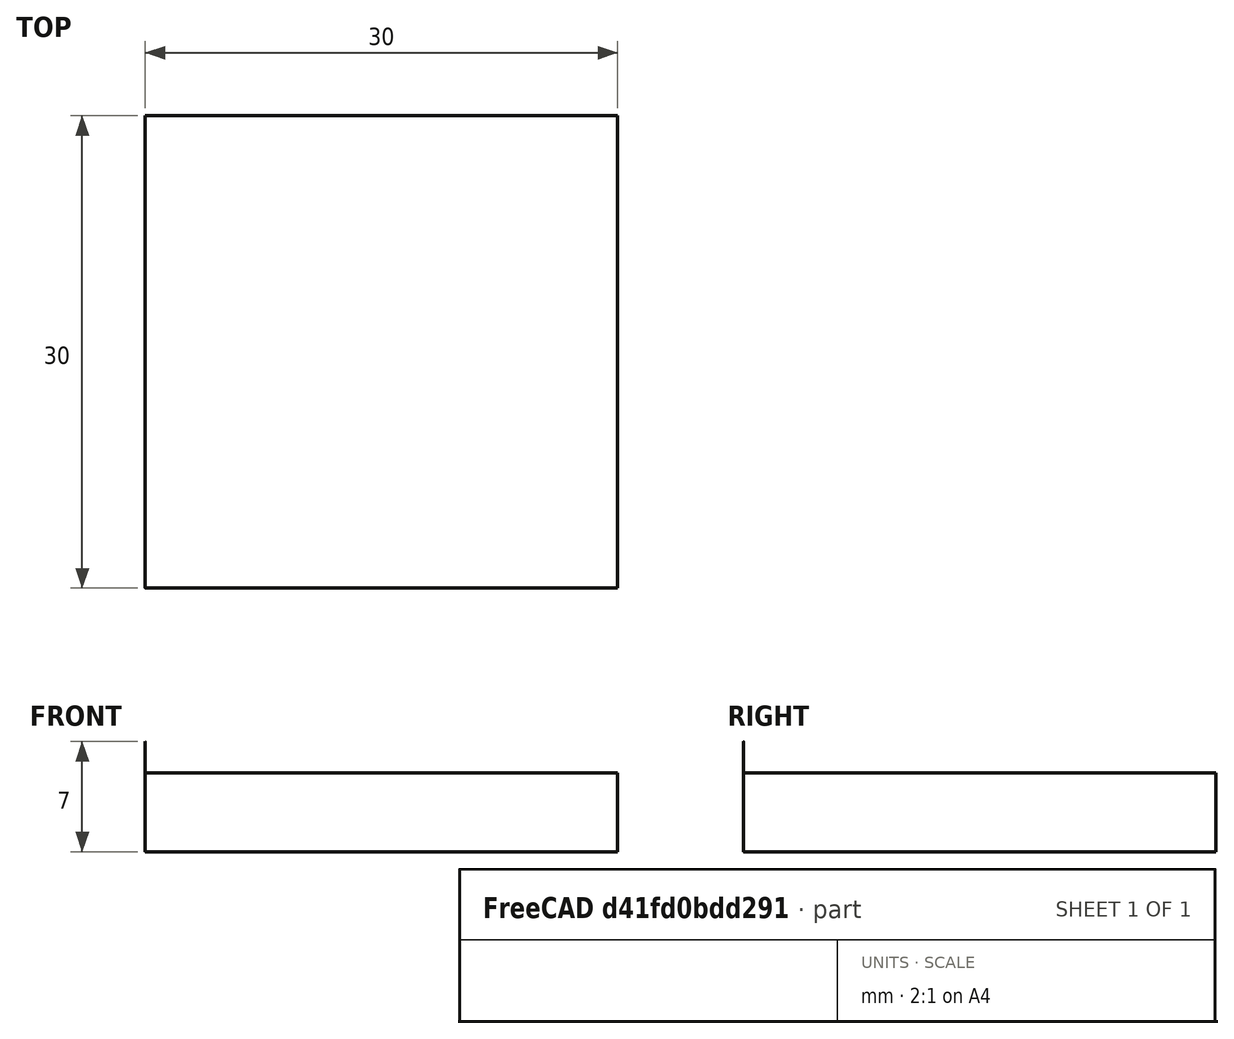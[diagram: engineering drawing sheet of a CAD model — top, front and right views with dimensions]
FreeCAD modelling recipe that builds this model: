
FCSTD DOCUMENT  (FreeCAD 1.0R39109 (Git))
Label: BoxWith2LargePockets
License: All rights reserved
LicenseURL: https://en.wikipedia.org/wiki/All_rights_reserved
objects: Path::FeaturePython×4, Part::Box×3, Part::FeaturePython×3, App::DocumentObjectGroup×3, Part::Cut×2, App::FeaturePython×1
note: 10 computed .brp shape members not serialized (recipe doc carries the construction recipe); baked Part::Feature solids carry a one-line shape summary decoded from their .brp

FEATURE [Part::Box] Box  label="Cube"
  AttacherType = Attacher::AttachEngine3D
  Height = 5
  Length = 30
  Width = 30
FEATURE [Part::Box] Box001  label="Cube001"
  AttacherType = Attacher::AttachEngine3D
  Height = 0.001
  Length = 10
  Placement = pos=(3,10,4.999) rot=(0,0,1;0rad)
  Width = 10
FEATURE [Part::Box] Box002  label="Cube002"
  AttacherType = Attacher::AttachEngine3D
  Height = 0.001
  Length = 10
  Placement = pos=(16,10,4.999) rot=(0,0,1;0rad)
  Width = 10
FEATURE [Part::Cut] Cut
  Base = -> Box
  Refine = true
  Tool = -> Box001
FEATURE [Part::Cut] Cut001
  Base = -> Cut
  Refine = true
  Tool = -> Box002
FEATURE [App::FeaturePython] SetupSheet  # Path/CAM operation (typed FeaturePython)
  ClearanceHeightExpression = OpStockZMax+SetupSheet.ClearanceHeightOffset
  ClearanceHeightOffset = 5
  CoolantMode = 0
  CoolantModes = None | Flood | Mist
  FinalDepthExpression = OpFinalDepth
  HorizRapid = 0
  SafeHeightExpression = OpStockZMax+SetupSheet.SafeHeightOffset
  SafeHeightOffset = 3
  StartDepthExpression = OpStartDepth
  StepDownExpression = OpToolDiameter
  VertRapid = 0
FEATURE [Part::FeaturePython] Clone  label="Model-Cut001"  # Draft clone (typed FeaturePython)
  AttacherType = Attacher::AttachEngine3D
  Fuse = false
  Objects = -> [Cut001]
  PathResource = Model
  Scale = (1,1,1)
FEATURE [App::DocumentObjectGroup] Model
  Group = -> [Clone]
FEATURE [Part::FeaturePython] ToolBit  label="Drill"  # Path/CAM toolbit (typed FeaturePython)
  BitPropertyNames = Chipload | Diameter | Flutes | Length | Material | TipAngle
  BitShape = <path>
  Chipload = 0
  Diameter = 0.005
  Flutes = 0
  Length = 7
  Material = 0
  ShapeName = drill
  TipAngle = 119
FEATURE [Path::FeaturePython] TC__Default_Tool  label="TC: Default Tool"  # Path/CAM operation (typed FeaturePython)
  HorizFeed = 0
  HorizRapid = 0
  SpindleDir = 0
  SpindleSpeed = 0
  Tool = -> ToolBit
  ToolNumber = 1
  VertFeed = 0
  VertRapid = 0
  expr: HorizRapid = SetupSheet.HorizRapid
  expr: VertRapid = SetupSheet.VertRapid
FEATURE [App::DocumentObjectGroup] Tools
  Group = -> [TC__Default_Tool]
FEATURE [Part::FeaturePython] Stock  # WARN: FeaturePython — macro-defined, semantics opaque (R4)
  Base = -> Model
  ExtXneg = 0.001
  ExtXpos = 0.001
  ExtYneg = 0.001
  ExtYpos = 0.001
  ExtZneg = 0.001
  ExtZpos = 0.001
  StockType = FromBase
FEATURE [Path::FeaturePython] Pocket_Shape  # Path/CAM operation (typed FeaturePython)
  Active = true
  AreaParams:
    Tolerance = 1e-07
    FitArcs = True
    Simplify = False
    CleanDistance = 0.0
    Accuracy = 0.01
    Unit = 1.0
    MinArcPoints = 4
    MaxArcPoints = 100
    ClipperScale = 10000000.0
    Fill = 0
    Coplanar = 0
    Reorient = True
    Outline = False
    Explode = False
    OpenMode = 0
    Deflection = 0.01
    SubjectFill = 0
    ClipFill = 0
    Offset = 0.0
    ExtraPass = 0
    Stepover = 0.0
    LastStepover = 0.0
    JoinType = 0
    EndType = 0
    MiterLimit = 2.0
    RoundPrecision = 0.0
    PocketMode = 1
    ToolRadius = 0.0025
    PocketExtraOffset = 0.0
    PocketStepover = 0.0025
    PocketLastStepover = 0.0
    FromCenter = True
    Angle = 0.0
    AngleShift = 0.0
    Shift = 0.0
    Thicken = False
    SectionCount = -1
    Stepdown = 1.0
    SectionOffset = 0.0
    SectionTolerance = 1e-06
    SectionMode = 2
    Project = False
  Base = -> [Clone]
  ClearanceHeight = 10.001
  CoolantMode = 0
  CutMode = 0
  CycleTime = Cycletime Error
  ExtensionCorners = true
  ExtensionLengthDefault = 0.0025
  ExtraOffset = 0
  FinalDepth = 4.999
  FinishDepth = 0
  KeepToolDown = false
  MinTravel = false
  OffsetPattern = 0
  OpFinalDepth = 4.999
  OpStartDepth = 5.001
  OpStockZMax = 5.001
  OpStockZMin = -0.001
  OpToolDiameter = 0.005
  PathParams = {'orientation': 1, 'feedrate': 0.0, 'feedrate_v': 0.0, 'verbose': True, 'resume_height': 8.001000000000001, 'retraction': 10.001000000000001, 'return_end': True, 'preamble': False, 'start': Vector (0.0, 0.0, 0.0)}
  PocketLastStepOver = 0
  SafeHeight = 8.001
  SplitArcs = false
  StartAt = 0
  StartDepth = 5.001
  StartPoint = (0,0,0)
  StepDown = 0.005
  StepOver = 50
  ToolController = -> TC__Default_Tool
  UseOutline = false
  UseRestMachining = false
  UseStartPoint = true
  ZigZagAngle = 0
  expr: ClearanceHeight = OpStockZMax + SetupSheet.ClearanceHeightOffset
  expr: ExtensionLengthDefault = OpToolDiameter / 2
  expr: FinalDepth = OpFinalDepth
  expr: SafeHeight = OpStockZMax + SetupSheet.SafeHeightOffset
  expr: StartDepth = OpStartDepth
  expr: StepDown = OpToolDiameter
FEATURE [Path::FeaturePython] Pocket_Shape001  # Path/CAM operation (typed FeaturePython)
  Active = true
  AreaParams:
    Tolerance = 1e-07
    FitArcs = True
    Simplify = False
    CleanDistance = 0.0
    Accuracy = 0.01
    Unit = 1.0
    MinArcPoints = 4
    MaxArcPoints = 100
    ClipperScale = 10000000.0
    Fill = 0
    Coplanar = 0
    Reorient = True
    Outline = False
    Explode = False
    OpenMode = 0
    Deflection = 0.01
    SubjectFill = 0
    ClipFill = 0
    Offset = 0.0
    ExtraPass = 0
    Stepover = 0.0
    LastStepover = 0.0
    JoinType = 0
    EndType = 0
    MiterLimit = 2.0
    RoundPrecision = 0.0
    PocketMode = 5
    ToolRadius = 0.0025
    PocketExtraOffset = 0.0
    PocketStepover = 0.0025
    PocketLastStepover = 0.0
    FromCenter = True
    Angle = 0.0
    AngleShift = 0.0
    Shift = 0.0
    Thicken = False
    SectionCount = -1
    Stepdown = 1.0
    SectionOffset = 0.0
    SectionTolerance = 1e-06
    SectionMode = 2
    Project = False
  Base = -> [Clone]
  ClearanceHeight = 10.001
  CoolantMode = 0
  CutMode = 0
  CycleTime = Cycletime Error
  ExtensionCorners = true
  ExtensionLengthDefault = 0.0025
  ExtraOffset = 0
  FinalDepth = 4.999
  FinishDepth = 0
  KeepToolDown = false
  MinTravel = false
  OffsetPattern = 3
  OpFinalDepth = 4.999
  OpStartDepth = 5.001
  OpStockZMax = 5.001
  OpStockZMin = -0.001
  OpToolDiameter = 0.005
  PathParams = {'orientation': 1, 'feedrate': 0.0, 'feedrate_v': 0.0, 'verbose': True, 'resume_height': 8.001000000000001, 'retraction': 10.001000000000001, 'return_end': True, 'preamble': False, 'start': Vector (0.0, 0.0, 0.0)}
  PocketLastStepOver = 0
  SafeHeight = 8.001
  SplitArcs = false
  StartAt = 0
  StartDepth = 5.001
  StartPoint = (0,0,0)
  StepDown = 0.005
  StepOver = 50
  ToolController = -> TC__Default_Tool
  UseOutline = false
  UseRestMachining = false
  UseStartPoint = true
  ZigZagAngle = 0
  expr: ClearanceHeight = OpStockZMax + SetupSheet.ClearanceHeightOffset
  expr: ExtensionLengthDefault = OpToolDiameter / 2
  expr: FinalDepth = OpFinalDepth
  expr: SafeHeight = OpStockZMax + SetupSheet.SafeHeightOffset
  expr: StartDepth = OpStartDepth
  expr: StepDown = OpToolDiameter
FEATURE [App::DocumentObjectGroup] Operations
  Group = -> [Pocket_Shape,Pocket_Shape001]
FEATURE [Path::FeaturePython] Job  # Path/CAM operation (typed FeaturePython)
  CycleTime = 00:00:00
  Fixtures = G54
  GeometryTolerance = 0.01
  JobType = 0
  Model = -> Model
  Operations = -> Operations
  OrderOutputBy = 0
  PostProcessor = 14
  SetupSheet = -> SetupSheet
  SplitOutput = false
  Stock = -> Stock
  Tools = -> Tools
note: 1 file-system path scrubbed to <path> (originals preserved in the JSON sidecar)
